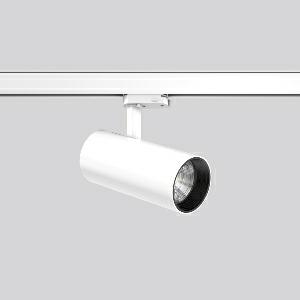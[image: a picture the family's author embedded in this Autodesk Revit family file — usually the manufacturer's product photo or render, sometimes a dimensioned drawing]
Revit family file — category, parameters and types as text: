
# Revit family: deecos_s_mini_742200_002_1_76_6521
name_source: partatom
category: Lighting Fixtures
units: mm (PartAtom-declared; Revit-internal decimal feet)

## family parameters
Cut with Voids When Loaded = No
Host = Face
Light Source = No
Part Type = Normal
Room Calculation Point = No
Round Connector Dimension = Use Diameter
Shared = No

## types (1)
- DEECOS S mini (1 x LED Modul 940, 2150 lm, 4000)
    Apparent Load = 20 VA
    Approval mark = CE
    CIE Flux Codes = 98 100 100 100 100
    Color Rendering = 92
    Color Temperature = 4000
    Default Elevation = 1800 mm
    Description = Series: DEECOS S mini
LED surface-mounted projector in modern design with no visible cooling ribs. Housing: die-cast aluminium, powder-coated. Rotation range: 356°. Swivel range: 90°. Black plastic ring and recessed LED to prevent glare from the side. Optical assembly with lens made of plastic (polycarbonate) for the best homogeneous light distribution - can be changed without tools. Best colour rendering index Ra>90. With adapter for RZB 3-circuit DALI tracks. Suitable for Track on ceiling, Wall track. High quality converter without flickering and stroboscopic effect. The following accessories can be mounted without use of tools: interchangeable lenses, decorative glasses, honeycomb louvre, clear and frosted diffusers, white interchangeable plastic ring. 
Colour: traffic white, matt (RAL 9016)
Diameter: 87 mm
Height: 214 mm
Lamp: LED
Socket: without socket
Colour temperature: 4000K
Colour rendering index (CRI): 92
System power: 20 W
Rated luminous flux: 2150 lm
Luminous efficiency: 108 lm/W
Control gear: Converter, dimmable, DALI
Protection class: I
Type of protection: IP 20
    Height = 214 mm
    Lamp = 1 x LED Modul 940
    Lamp Light Flux = 2150 lm
    Lamp count = 1
    Length = 87 mm
    Lifetime = 50000 h
    Luminous efficacy = 108 lm/W
    Manufacturer = RZB
    ModVariant = No
    Model = 742200.002.1.76
    Mounting Place = Ceiling
    Mounting Type = Rail mounted
    Number of Poles = 1
    OnlyDefault = Yes
    Power Factor = 1
    Product Name = DEECOS S mini
    Product group = Track mounted projectors
    ProductGroupID = 301
    Protection Class = Protection class I
    Protection Degree = IP 20
    RLX_Detail_Level = 1
    RLX_Emergency_Light_Flux = 0 lm
    RLX_Emergency_Type = 0
    RLX_Emergency_Type_DB = No
    RlxData = <blob elided: 36077 chars, md5=ee4b5495>
    Socket = socket
    Standby Power = 0 W
    System Light Flux = 2150 lm
    System Power = 20 W
    Type Comments = Product without accessories
    Type Image = 741930.002.jpg
    URL = http://relux.com
    VarID = ---
    Voltage = 230 V
    Voltage Range = 220-240 V
    Weight = 0.00 kg
    Width = 0 mm  [stored 0 ft]

note: [stored X ft] marks values corroborated as IEEE doubles in the binary element streams (Revit-internal decimal feet)

## geometry (parser evidence)
native form markers: Blend x4, Sweep x13
no freeform markers — native parametric forms only
